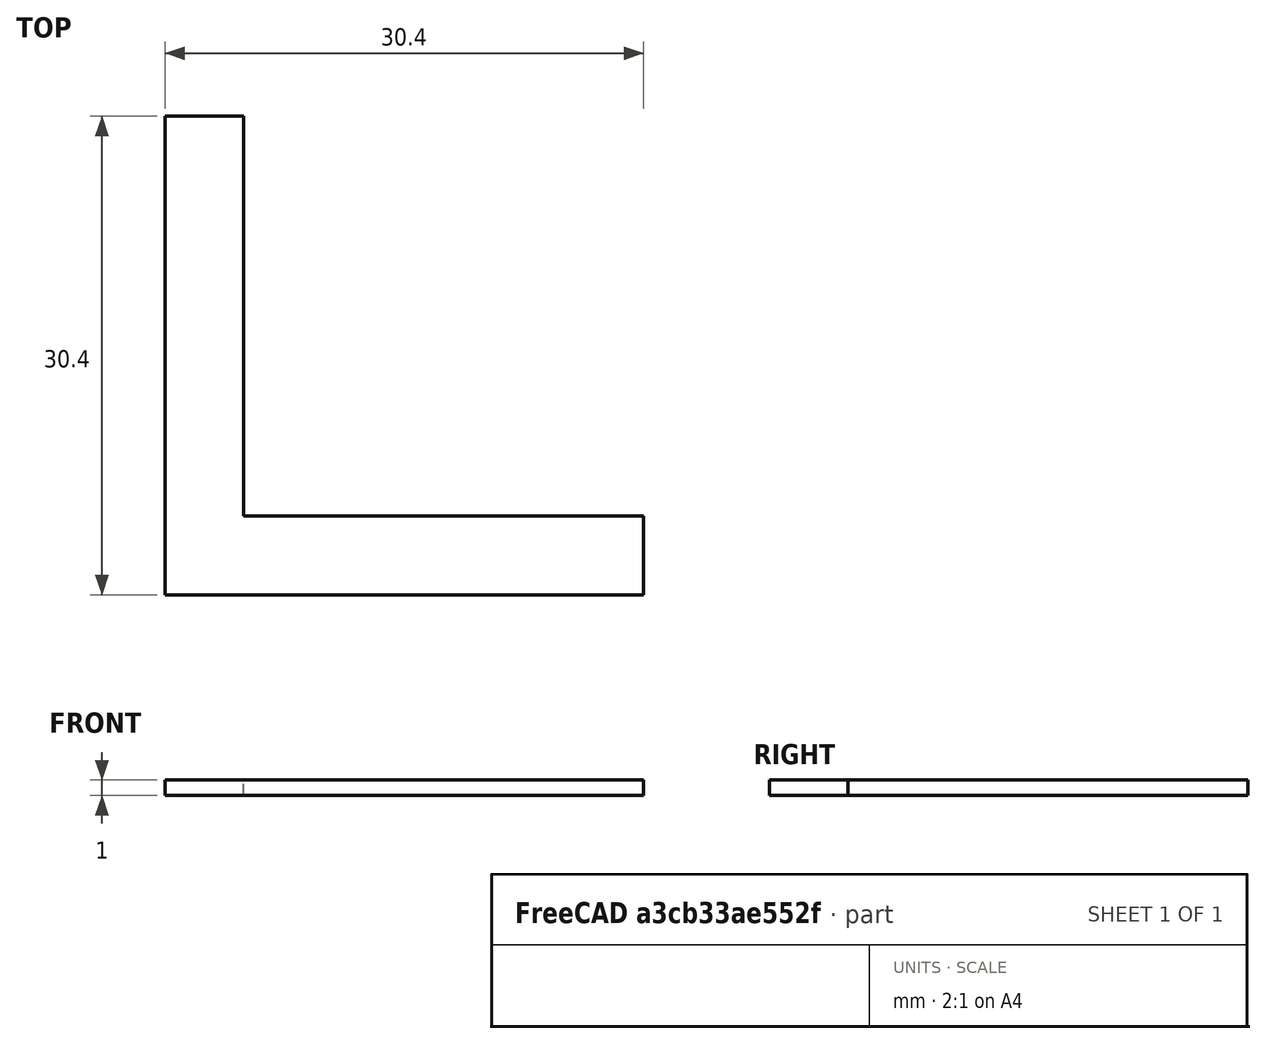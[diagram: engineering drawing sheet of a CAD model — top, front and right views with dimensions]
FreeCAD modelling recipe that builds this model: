
FCSTD DOCUMENT  (FreeCAD 1.0R38641 +468 (Git))
Label: scan-helper
License: All rights reserved
LicenseURL: http://en.wikipedia.org/wiki/All_rights_reserved
objects: Sketcher::SketchObject×1, PartDesign::Pad×1, PartDesign::Body×1, App::Part×1
note: 6 computed .brp shape members not serialized (recipe doc carries the construction recipe); baked Part::Feature solids carry a one-line shape summary decoded from their .brp

FEATURE [Sketcher::SketchObject] Sketch
  ArcFitTolerance = 1e-06
  AttachmentSupport = -> [XY_Plane001]
  FullyConstrained = true
  MakeInternals = false
  MapMode = 5
  sketch-geometry (6):
    g0: LineSegment StartX=0 StartY=30.4 StartZ=0 EndX=5 EndY=30.4 EndZ=0
    g1: LineSegment StartX=5 StartY=30.4 StartZ=0 EndX=5 EndY=5 EndZ=0
    g2: LineSegment StartX=5 StartY=5 StartZ=0 EndX=30.4 EndY=5 EndZ=0
    g3: LineSegment StartX=30.4 StartY=5 StartZ=0 EndX=30.4 EndY=0 EndZ=0
    g4: LineSegment StartX=30.4 StartY=0 StartZ=0 EndX=0 EndY=0 EndZ=0
    g5: LineSegment StartX=0 StartY=0 StartZ=0 EndX=0 EndY=30.4 EndZ=0
  constraints (18):
    c: PointOnObject(g0,g-2)
    c: Horizontal(g0)
    c: Coincident(g0,g1)
    c: Vertical(g1)
    c: Coincident(g1,g2)
    c: Horizontal(g2)
    c: Coincident(g2,g3)
    c: PointOnObject(g3,g-1)
    c: Coincident(g3,g4)
    c: PointOnObject(g4,g-1)
    c: Coincident(g4,g5)
    c: Coincident(g5,g0)
    c: Vertical(g5)
    c: Vertical(g3)
    c: Equal(g0,g3)
    c: Equal(g1,g2)
    c: Distance(g3,g3) = 5
    c: DistanceX(g2,g2) = 25.4
FEATURE [PartDesign::Pad] Pad
  Direction = (0,0,1)
  Length = 1
  Length2 = 10
  Profile = -> Sketch
  ReferenceAxis = -> Sketch [N_Axis]
  Suppressed = false
  Type = 0
FEATURE [PartDesign::Body] Body
  AllowCompound = false
  Group = -> [Sketch,Pad]
  Origin = -> Origin001
  Tip = -> Pad
FEATURE [App::Part] Part
  Group = -> [Body]
  Origin = -> Origin
